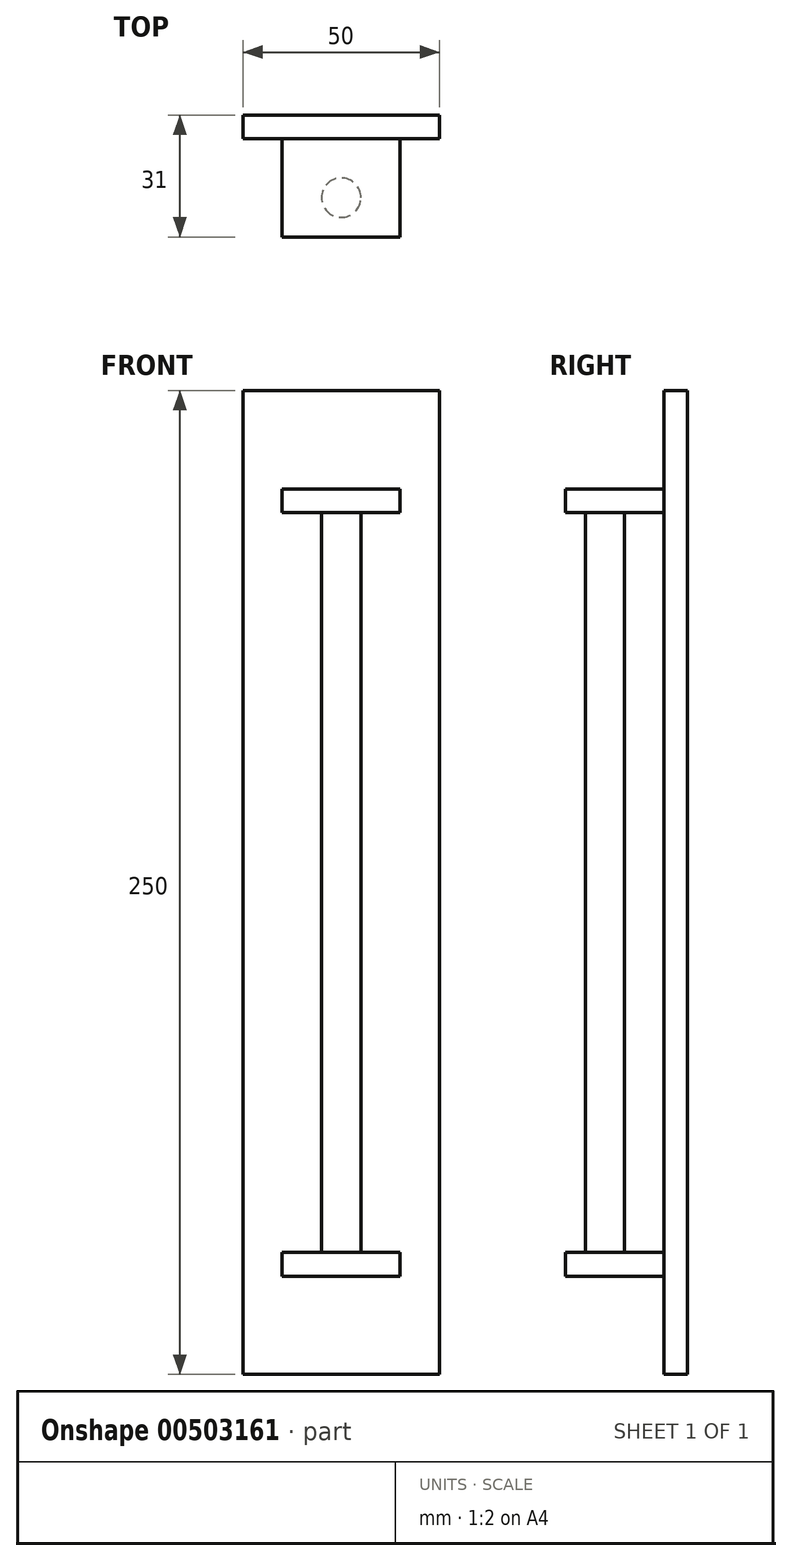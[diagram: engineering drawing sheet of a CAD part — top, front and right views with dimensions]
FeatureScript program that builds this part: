
annotation { "Feature Type Name" : "Feature", "Feature Type Description" : "" }
export const myFeature = defineFeature(function(context is Context, id is Id, definition is map)
    precondition{}
    {
        {
            var Q0;
            Q0=qCreatedBy(makeId("Front.planeOp"),FACE);
            var sketch = newSketch(context, id + "F0", { "sketchPlane" : qUnion([Q0])});
            skLineSegment(sketch, "E0.bottom", {"start": v(25, 125) * mm, "end": v(-25, 125) * mm});
            skLineSegment(sketch, "E0.top", {"start": v(25, -125) * mm, "end": v(-25, -125) * mm});
            skLineSegment(sketch, "E0.left", {"start": v(25, 125) * mm, "end": v(25, -125) * mm});
            skLineSegment(sketch, "E0.right", {"start": v(-25, 125) * mm, "end": v(-25, -125) * mm});
            skPoint(sketch, "E0.middle", {"position": v(0, 0) * mm});
            skSolve(sketch);
        }
        {
            var Q0;
            Q0=makeQuery(id+"F0.imprint","IMPRINT",FACE,{"disambiguationData":[TD([[makeQuery(id+"F0.imprint","IMPRINT",EDGE,{"derivedFrom":sQuery(id+"F0.wireOp",EDGE,"E0.bottom")}),1.0]])]});
            extrude(context, id + "F1", {"entities" : qUnion([Q0]), "depth" : 6 * mm});
        }
        {
            var Q0;
            Q0=makeQuery(id+"F1.opExtrude","CAP_FACE",FACE,{"disambiguationData":[OSD([sQuery(id+"F0.wireOp",EDGE,"E0.bottom"),sQuery(id+"F0.wireOp",EDGE,"E0.top"),sQuery(id+"F0.wireOp",EDGE,"E0.left"),sQuery(id+"F0.wireOp",EDGE,"E0.right")])],"isStart":false});
            var sketch = newSketch(context, id + "F2", { "sketchPlane" : qUnion([Q0])});
            skLineSegment(sketch, "E1", {"start": v(0, 125) * mm, "end": v(0, 100) * mm, "construction": true});
            skPoint(sketch, "E1.endSnap0", {"position": v(0, 125) * mm});
            skLineSegment(sketch, "E2", {"start": v(0, -125) * mm, "end": v(0, -100) * mm, "construction": true});
            skLineSegment(sketch, "E3", {"start": v(0, 100) * mm, "end": v(15, 100) * mm, "construction": true});
            skLineSegment(sketch, "E4", {"start": v(15, 100) * mm, "end": v(0, 100) * mm, "construction": true});
            skLineSegment(sketch, "E5", {"start": v(0, 100) * mm, "end": v(-15, 100) * mm, "construction": true});
            skLineSegment(sketch, "E6", {"start": v(0, -100) * mm, "end": v(-15, -100) * mm, "construction": true});
            skLineSegment(sketch, "E7", {"start": v(-15, -100) * mm, "end": v(0, -100) * mm, "construction": true});
            skLineSegment(sketch, "E8", {"start": v(0, -100) * mm, "end": v(15, -100) * mm, "construction": true});
            skLineSegment(sketch, "E9.bottom", {"start": v(-15, -100) * mm, "end": v(15, -100) * mm});
            skLineSegment(sketch, "E9.top", {"start": v(-15, -94) * mm, "end": v(15, -94) * mm});
            skLineSegment(sketch, "E9.left", {"start": v(-15, -100) * mm, "end": v(-15, -94) * mm});
            skLineSegment(sketch, "E9.right", {"start": v(15, -100) * mm, "end": v(15, -94) * mm});
            skLineSegment(sketch, "E10.bottom", {"start": v(-15, 100) * mm, "end": v(15, 100) * mm});
            skLineSegment(sketch, "E10.top", {"start": v(-15, 94) * mm, "end": v(15, 94) * mm});
            skLineSegment(sketch, "E10.left", {"start": v(-15, 100) * mm, "end": v(-15, 94) * mm});
            skLineSegment(sketch, "E10.right", {"start": v(15, 100) * mm, "end": v(15, 94) * mm});
            skSolve(sketch);
        }
        {
            var Q0;
            Q0=makeQuery(id+"F2.imprint","IMPRINT",FACE,{"disambiguationData":[TD([[makeQuery(id+"F2.imprint","IMPRINT",EDGE,{"derivedFrom":sQuery(id+"F2.wireOp",EDGE,"E10.bottom")}),-1.0]])]});
            var Q1;
            Q1=makeQuery(id+"F2.imprint","IMPRINT",FACE,{"disambiguationData":[TD([[makeQuery(id+"F2.imprint","IMPRINT",EDGE,{"derivedFrom":sQuery(id+"F2.wireOp",EDGE,"E9.bottom")}),1.0]])]});
            extrude(context, id + "F3", {"entities" : qUnion([Q0, Q1]), "operationType" : NewBodyOperationType.ADD, "depth" : 25 * mm});
        }
        {
            var Q0;
            Q0=makeQuery(id+"F3.opExtrude","SWEPT_FACE",FACE,{"disambiguationData":[OSD([sQuery(id+"F2.wireOp",EDGE,"E10.top")])]});
            var sketch = newSketch(context, id + "F4", { "sketchPlane" : qUnion([Q0])});
            skLineSegment(sketch, "E11", {"start": v(0, 31) * mm, "end": v(0, 6) * mm, "construction": true});
            skLineSegment(sketch, "E12", {"start": v(-15, 31) * mm, "end": v(-15, 21) * mm, "construction": true});
            skLineSegment(sketch, "E13", {"start": v(-15, 21) * mm, "end": v(15, 21) * mm, "construction": true});
            skCircle(sketch, "E14", {"center": v(0, 21) * mm, "radius": 5 * mm});
            skSolve(sketch);
        }
        {
            var Q0;
            Q0=qSketchRegion(id+"F4",true);
            extrude(context, id + "F5", {"entities" : qUnion([Q0]), "operationType" : NewBodyOperationType.ADD, "endBound" : BoundingType.UP_TO_NEXT, "depth" : 25 * mm});
        }
    });
